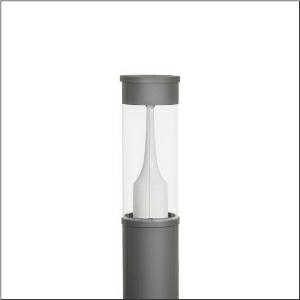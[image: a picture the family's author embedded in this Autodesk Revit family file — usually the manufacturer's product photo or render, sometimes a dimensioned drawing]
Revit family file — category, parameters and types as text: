
# Revit family: city-light_120_iq___p1_0a_5xa5285lf14h_baf3
name_source: partatom
category: Lighting Fixtures
units: mm (PartAtom-declared; Revit-internal decimal feet)

## family parameters
Cut with Voids When Loaded = No
Host = Face
Light Source = No
Part Type = Normal
Room Calculation Point = No
Round Connector Dimension = Use Diameter
Shared = No

## types (1)
- --- (1 x LED, 1510 lm, 10 W, 4000K)
    Apparent Load = 10 VA
    CIE Flux Codes = 32 61 90 93 100
    Color Rendering = 70
    Color Temperature = 4000K
    Default Elevation = 1800 mm
    Description = City-Light 120 iQ, bollard luminaire, Module 540 iQ-SR, primary light control with 3 zone facetted reflector, of plastic, silver coated, highly specular, structured, primary optical cover: cover, of PMMA, transparent, partly coated, light distribution: P1.0a, primary light characteristic: strongly asymmetric, LED, High Power LED, rated luminous flux: 1.510lm, luminous efficacy: 151lm/W, light colour: 740, colour temperature: 4000K, control gear: iQ Street-Remote, control: pre-setting: logarithmic dimming characteristic, Street-Remote, Auto-Match, Temp-Guard, Lumen-Switch, Night-Set, Smart-Wire, Light-Fading, Desk-Remote (wireless, voltage-free reading and setting of iQ features in the workshop via application-optimized NFC function/RFID function), optimised constant luminous flux control (CLO 2.0), with terminal, 6-pole, max. 2.5mm², mains connection: 230..240V, AC, 50/60Hz, start of lifetime: 10W, end of service life: 10W, reduction: 5W, luminaire housing, cylindrical, of extruded aluminium section, coated, Siteco® metallic grey (DB 702S), length: 1.200mm, diameter: 200mm, Module 540 iQ-SR, traffic white (RAL 9016), equipment: standard, protection rating (complete): IP54, insulation class (complete): insulation class II (safety insulation), certification: CE, ENEC, VDE, packaging unit: 1 piece

Light Distribution: P1.0a
    Height = 500 mm
    Lamp = 1 x LED
    Lamp Light Flux = 1510 lm
    Lamp Power = 10 W
    Lamp count = 1
    Length = 200 mm  [stored 0.656168 ft]
    Luminous efficacy = 151 lm/W
    Manufacturer = Siteco
    ModVariant = No
    Model = 5XA5285LF14H
    Mounting Place = Floor
    Mounting Type = Freestanding
    Number of Poles = 1
    OnlyDefault = Yes
    Power Factor = 1
    Product Name = City-Light 120 iQ | P1.0a
    Product group = bollard luminaire
    ProductGroupID = 1304
    Protection Class = Protection class II
    Protection Degree = IP 54
    RLX_Detail_Level = 1
    RLX_Emergency_Light_Flux = 0 lm
    RLX_Emergency_Type = 0
    RLX_Emergency_Type_DB = No
    RlxData = <blob elided: 52537 chars, md5=6af0135b>
    Socket = socket
    Standby Power = 0 W
    System Light Flux = 1510 lm
    System Power = 10 W
    Type Comments = factory setting: luminous flux: 100 % | dim-lin: 254 | 401 mA
    Type Image = l_1006922.jpg
    URL = http://relux.com
    VarID = @adj_181029
    Voltage = 0 V
    Weight = 0.00 kg
    Width = 0 mm  [stored 0 ft]

note: [stored X ft] marks values corroborated as IEEE doubles in the binary element streams (Revit-internal decimal feet)

## geometry (parser evidence)
native form markers: Blend x4, Sweep x13
no freeform markers — native parametric forms only
